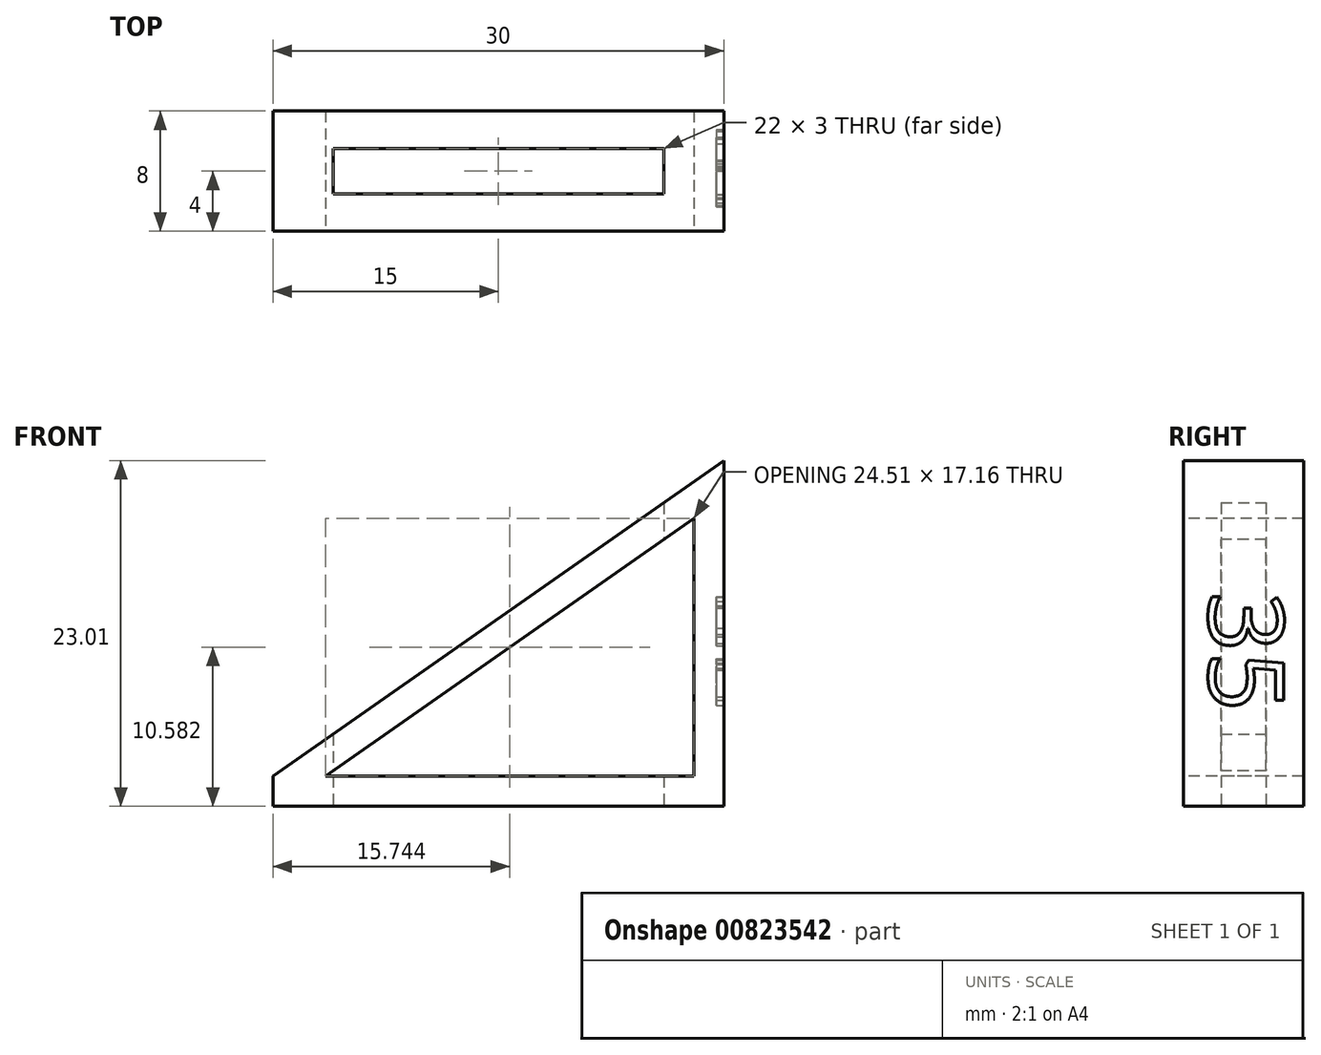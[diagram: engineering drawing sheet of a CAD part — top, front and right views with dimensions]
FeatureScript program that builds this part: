
annotation { "Feature Type Name" : "Feature", "Feature Type Description" : "" }
export const myFeature = defineFeature(function(context is Context, id is Id, definition is map)
    precondition{}
    {
        {
            var Q0;
            Q0=qCreatedBy(makeId("Top.planeOp"),FACE);
            var sketch = newSketch(context, id + "F0", { "sketchPlane" : qUnion([Q0])});
            skLineSegment(sketch, "E0.bottom", {"start": v(-15, 4) * mm, "end": v(15, 4) * mm});
            skLineSegment(sketch, "E0.top", {"start": v(-15, -4) * mm, "end": v(15, -4) * mm});
            skLineSegment(sketch, "E0.left", {"start": v(-15, 4) * mm, "end": v(-15, -4) * mm});
            skLineSegment(sketch, "E0.right", {"start": v(15, 4) * mm, "end": v(15, -4) * mm});
            skPoint(sketch, "E0.middle", {"position": v(0, 0) * mm});
            skLineSegment(sketch, "E1.bottom", {"start": v(-11, 1.5) * mm, "end": v(11, 1.5) * mm});
            skLineSegment(sketch, "E1.top", {"start": v(-11, -1.5) * mm, "end": v(11, -1.5) * mm});
            skLineSegment(sketch, "E1.left", {"start": v(-11, 1.5) * mm, "end": v(-11, -1.5) * mm});
            skLineSegment(sketch, "E1.right", {"start": v(11, 1.5) * mm, "end": v(11, -1.5) * mm});
            skSolve(sketch);
        }
        {
            var Q0;
            Q0=makeQuery(id+"F0.imprint","IMPRINT",FACE,{"disambiguationData":[TD([[makeQuery(id+"F0.imprint","IMPRINT",EDGE,{"derivedFrom":sQuery(id+"F0.wireOp",EDGE,"E0.bottom")}),-1.0]])]});
            extrude(context, id + "F1", {"entities" : qUnion([Q0]), "depth" : 2 * mm, "offsetDistance" : 25 * mm});
        }
        {
            var Q0;
            Q0=makeQuery(id+"F1.opExtrude","CAP_FACE",FACE,{"disambiguationData":[OSD([sQuery(id+"F0.wireOp",EDGE,"E0.bottom"),sQuery(id+"F0.wireOp",EDGE,"E0.top"),sQuery(id+"F0.wireOp",EDGE,"E0.left"),sQuery(id+"F0.wireOp",EDGE,"E0.right"),sQuery(id+"F0.wireOp",EDGE,"E1.bottom"),sQuery(id+"F0.wireOp",EDGE,"E1.top"),sQuery(id+"F0.wireOp",EDGE,"E1.left"),sQuery(id+"F0.wireOp",EDGE,"E1.right")])],"isStart":false});
            var sketch = newSketch(context, id + "F2", { "sketchPlane" : qUnion([Q0])});
            skLineSegment(sketch, "E2.bottom", {"start": v(-15, 4) * mm, "end": v(-13, 4) * mm});
            skLineSegment(sketch, "E2.top", {"start": v(-15, -4) * mm, "end": v(-13, -4) * mm});
            skLineSegment(sketch, "E2.left", {"start": v(-15, 4) * mm, "end": v(-15, -4) * mm});
            skLineSegment(sketch, "E2.right", {"start": v(-13, 4) * mm, "end": v(-13, -4) * mm});
            skSolve(sketch);
        }
        {
            var Q0;
            Q0=makeQuery(id+"F1.opExtrude","SWEPT_FACE",FACE,{"disambiguationData":[OSD([sQuery(id+"F0.wireOp",EDGE,"E0.top")])]});
            var sketch = newSketch(context, id + "F3", { "sketchPlane" : qUnion([Q0])});
            skLineSegment(sketch, "E3", {"start": v(15, 2) * mm, "end": v(15, 23) * mm});
            skLineSegment(sketch, "E4", {"start": v(15, 23) * mm, "end": v(-15, 2) * mm});
            skLineSegment(sketch, "E5", {"start": v(15, 2) * mm, "end": v(13, 2) * mm});
            skLineSegment(sketch, "E6", {"start": v(13, 2) * mm, "end": v(13, 19.16) * mm});
            skLineSegment(sketch, "E7", {"start": v(-11.51, 2) * mm, "end": v(13, 19.16) * mm});
            skSolve(sketch);
        }
        {
            var Q0;
            Q0=makeQuery(id+"F3.imprint","IMPRINT",FACE,{"disambiguationData":[TD([[makeQuery(id+"F3.imprint","IMPRINT",EDGE,{"derivedFrom":sQuery(id+"F3.wireOp",EDGE,"E3")}),1.0]])]});
            extrude(context, id + "F4", {"entities" : qUnion([Q0]), "oppositeDirection" : true, "depth" : 8 * mm, "offsetDistance" : 25 * mm});
        }
        {
            var Q0;
            Q0=makeQuery(id+"F2.imprint","IMPRINT",FACE,{"disambiguationData":[TD([[makeQuery(id+"F2.imprint","IMPRINT",EDGE,{"derivedFrom":makeQuery(id+"F1.opExtrude","CAP_EDGE",EDGE,{"disambiguationData":[OSD([sQuery(id+"F0.wireOp",EDGE,"E1.bottom")])],"isStart":false})}),-1.0]])]});
            extrude(context, id + "F5", {"entities" : qUnion([Q0]), "operationType" : NewBodyOperationType.REMOVE, "depth" : 25 * mm, "offsetDistance" : 25 * mm});
        }
        {
            var Q0;
            Q0=makeQuery(id+"F1.opExtrude","SWEPT_BODY",BODY,{"disambiguationData":[OSD([sQuery(id+"F0.wireOp",EDGE,"E0.bottom"),sQuery(id+"F0.wireOp",EDGE,"E0.top"),sQuery(id+"F0.wireOp",EDGE,"E0.left"),sQuery(id+"F0.wireOp",EDGE,"E0.right"),sQuery(id+"F0.wireOp",EDGE,"E1.bottom"),sQuery(id+"F0.wireOp",EDGE,"E1.top"),sQuery(id+"F0.wireOp",EDGE,"E1.left"),sQuery(id+"F0.wireOp",EDGE,"E1.right")])]});
            var Q1;
            Q1=makeQuery(id+"F4.opExtrude","SWEPT_BODY",BODY,{"disambiguationData":[OSD([sQuery(id+"F0.wireOp",EDGE,"E0.top"),sQuery(id+"F3.wireOp",EDGE,"E3"),sQuery(id+"F3.wireOp",EDGE,"E4"),sQuery(id+"F3.wireOp",EDGE,"E5"),sQuery(id+"F3.wireOp",EDGE,"E6"),sQuery(id+"F3.wireOp",EDGE,"E7")])]});
            booleanBodies(context, id + "F6", {"operationType" : BooleanOperationType.UNION, "tools" : qUnion([Q0, Q1])});
        }
        {
            var Q0;
            Q0=makeQuery(id+"F6.opBoolean","MERGE",FACE,{"derivedFrom":[makeQuery(id+"F1.opExtrude","SWEPT_FACE",FACE,{"disambiguationData":[OSD([sQuery(id+"F0.wireOp",EDGE,"E0.right")])]}),makeQuery(id+"F4.opExtrude","SWEPT_FACE",FACE,{"disambiguationData":[OSD([sQuery(id+"F3.wireOp",EDGE,"E3")])]})]});
            var sketch = newSketch(context, id + "F7", { "sketchPlane" : qUnion([Q0])});
            skText(sketch, "E8", { "text": "35", "fontName": "OpenSans-Regular.ttf"});
            const initialGuessF7  = {"E8": [-0.0023, 0.01426, 0, -1, 0.005]};
            skSetInitialGuess(sketch, initialGuessF7);
            skSolve(sketch);
        }
        {
            var Q0;
            Q0 = qSketchRegion(id + "F7", true);
            extrude(context, id + "F8", {"entities" : qUnion([Q0]), "operationType" : NewBodyOperationType.REMOVE, "oppositeDirection" : true, "depth" : .5 * mm, "offsetDistance" : 25 * mm});
        }
    });
